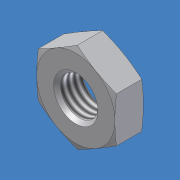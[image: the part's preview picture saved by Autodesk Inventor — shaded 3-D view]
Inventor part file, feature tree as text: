
AUTODESK INVENTOR PART (.ipt)
format: ipt  version: 2012 (Build 160160000, 160)  size: 127,488 bytes
history: native  units: mm (DEFAULTED — no unit token found)
features: other x70, sketch x3, revolve x2, extrude x1, thread x1
ambient origin geometry x8: Origin, YZ Plane, XZ Plane, XY Plane, X Axis, Y Axis, Z Axis, Center Point
bodies: Solid1 (feature_tree)
feature tree (77):
  sketch  "Sketch_8"  dims[d0=360.0deg d1=4.064mm d2=0.0mm]
  sketch  "Sketch_10"  dims[d3=360.0deg d4=3.08102mm d5=0.0mm]
  revolve  "Revolution1"  [1 undecoded]
  extrude  "Extrusion1"  Depth=3.08102mm TaperAngle=0.0deg
  revolve  "Revolution2"  [1 undecoded]
  thread  "Thread1"  [1 undecoded]
  other  "NUT_XY"
  other  "NUT_YZ"
  other  "NUT_ZX"
  other  "NUT_X"
  other  "NUT_Y"
  other  "NUT_Z"
  other  "NUT_Center"
  other  "a1_XY"
  other  "a1_YZ"
  other  "a1_ZX"
  other  "a1_X"
  other  "a1_Y"
  other  "a1_Z"
  other  "a1_Center"
  other  "a2_XY"
  other  "a2_YZ"
  other  "a2_ZX"
  other  "a2_X"
  other  "a2_Y"
  other  "a2_Z"
  other  "a2_Center"
  other  "b1_XY"
  other  "b1_YZ"
  other  "b1_ZX"
  other  "b1_X"
  other  "b1_Y"
  other  "b1_Z"
  other  "b1_Center"
  other  "b2_XY"
  other  "b2_YZ"
  other  "b2_ZX"
  other  "b2_X"
  other  "b2_Y"
  other  "b2_Z"
  other  "b2_Center"
  other  "e_XY"
  other  "e_YZ"
  other  "e_ZX"
  other  "e_X"
  other  "e_Y"
  other  "e_Z"
  other  "e_Center"
  other  "th1_XY"
  other  "th1_YZ"
  other  "th1_ZX"
  other  "th1_X"
  other  "th1_Y"
  other  "th1_Z"
  other  "th1_Center"
  other  "th2_XY"
  other  "th2_YZ"
  other  "th2_ZX"
  other  "th2_X"
  other  "th2_Y"
  other  "th2_Z"
  other  "th2_Center"
  other  "ol1_XY"
  other  "ol1_YZ"
  other  "ol1_ZX"
  other  "ol1_X"
  other  "ol1_Y"
  other  "ol1_Z"
  other  "ol1_Center"
  other  "ol2_XY"
  other  "ol2_YZ"
  other  "ol2_ZX"
  other  "ol2_X"
  other  "ol2_Y"
  other  "ol2_Z"
  other  "ol2_Center"
  sketch  "Sketch_11"
note: 3 required parameter values undecoded (feature->parameter linkage not recoverable at this tier; creation-order binding heuristic only, values carry confidence <= 0.55)